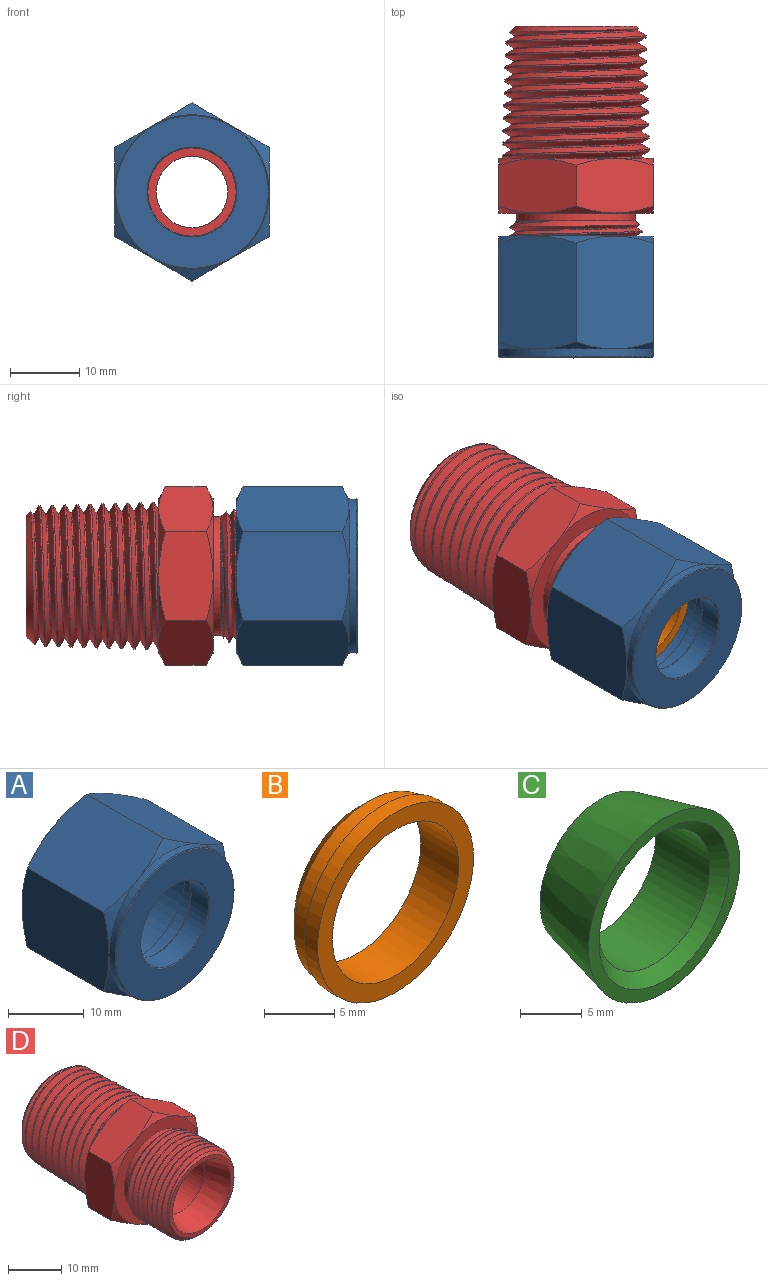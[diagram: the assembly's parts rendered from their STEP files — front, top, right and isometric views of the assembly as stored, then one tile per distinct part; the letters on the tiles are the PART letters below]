
ASSEMBLY  parts=4 mates=3
PART A: 29 faces, bbox 25.7x17.5x25.7 mm
  f0: plane 22.23x22.23mm, normal (0,1,0), area 102.9mm2, adj f2,f3,f4,f5,f6,f7,f22
  f1: plane 21.97x21.97mm, normal (0,-1,0), area 247.3mm2, adj f27,f28
  f2: cone r=12.83mm half-angle=60deg, axis (0,-1,0), area 7.7mm2, adj f0,f9,f10
  f3: cone r=12.83mm half-angle=60deg, axis (0,-1,0), area 7.7mm2, adj f0,f10,f11
  f4: cone r=12.83mm half-angle=60deg, axis (0,-1,0), area 7.7mm2, adj f0,f11,f12
  f5: cone r=12.83mm half-angle=60deg, axis (0,-1,0), area 7.7mm2, adj f0,f12,f13
  f6: cone r=12.83mm half-angle=60deg, axis (0,-1,0), area 7.7mm2, adj f0,f8,f13
  f7: cone r=12.83mm half-angle=60deg, axis (0,-1,0), area 7.7mm2, adj f0,f8,f9
  f8: plane 16.26x11.11mm, normal (0.5,0,0.87), area 199.9mm2, adj f6,f7,f9,f13,f15,f20
  f9: plane 16.26x12.84mm, normal (1,0,0), area 199.9mm2, adj f2,f7,f8,f10,f19,f20
  f10: plane 16.26x11.11mm, normal (0.5,0,-0.87), area 199.9mm2, adj f2,f3,f9,f11,f18,f19
  f11: plane 16.26x11.11mm, normal (-0.5,0,-0.87), area 199.9mm2, adj f3,f4,f10,f12,f17,f18
  f12: plane 16.26x12.84mm, normal (-1,0,0), area 199.9mm2, adj f4,f5,f11,f13,f16,f17
  f13: plane 16.26x11.11mm, normal (-0.5,0,0.87), area 199.9mm2, adj f5,f6,f8,f12,f15,f16
  f14: cylinder r=11.11mm len=22.23mm, axis (0,-1,0), area 79.8mm2, adj f15,f16,f17,f18,f19,f20,f28
  f15: cone r=11.11mm half-angle=60deg, axis (0,1,0), area 7.7mm2, adj f8,f13,f14
  f16: cone r=11.11mm half-angle=60deg, axis (0,1,0), area 7.7mm2, adj f12,f13,f14
  f17: cone r=11.11mm half-angle=60deg, axis (0,1,0), area 7.7mm2, adj f11,f12,f14
  f18: cone r=11.11mm half-angle=60deg, axis (0,1,0), area 7.7mm2, adj f10,f11,f14
  f19: cone r=11.11mm half-angle=60deg, axis (0,1,0), area 7.7mm2, adj f9,f10,f14
  f20: cone r=11.11mm half-angle=60deg, axis (0,1,0), area 7.7mm2, adj f8,f9,f14
  f21: cylinder r=6.35mm len=12.7mm, axis (0,-1,0), area 129.7mm2, adj f26,f27
  f22: cylinder r=9.53mm len=19.05mm, axis (0,-1,0), area 629.3mm2, adj f0,f23
  f23: plane 19.05x19.05mm, normal (0,1,0), area 36.7mm2, adj f22,f24
  f24: cylinder r=8.89mm len=17.78mm, axis (0,-1,0), area 195.8mm2, adj f23,f25
  f25: plane 17.78x17.78mm, normal (0,1,0), area 116.5mm2, adj f24,f26
  f26: cone r=6.48mm half-angle=45deg, axis (0,1,0), area 7.2mm2, adj f21,f25
  f27: cone r=6.35mm half-angle=45deg, axis (0,-1,0), area 7.2mm2, adj f1,f21
  f28: cone r=10.99mm half-angle=45deg, axis (0,1,0), area 12.5mm2, adj f1,f14
PART B: 6 faces, bbox 15.7x3.8x15.7 mm
  f0: plane 15.67x15.67mm, normal (0,-1,0), area 66.2mm2, adj f1,f5
  f1: cylinder r=7.84mm len=15.67mm, axis (0,-1,0), area 62.5mm2, adj f0,f2
  f2: plane 15.67x15.67mm, normal (0,1,0), area 17.7mm2, adj f1,f3
  f3: cylinder r=7.47mm len=14.94mm, axis (0,-1,0), area 66.7mm2, adj f2,f4
  f4: cone r=6.35mm half-angle=45deg, axis (0,-1,0), area 68.6mm2, adj f3,f5
  f5: cylinder r=6.35mm len=12.7mm, axis (0,-1,0), area 152mm2, adj f0,f4
PART C: 5 faces, bbox 17.3x7.3x17.3 mm
  f0: cone r=6.88mm half-angle=13.7deg, axis (0,-1,0), area 367.6mm2, adj f1,f4
  f1: plane 17.32x17.32mm, normal (0,-1,0), area 60.5mm2, adj f0,f2
  f2: cone r=7.47mm half-angle=45deg, axis (0,-1,0), area 68.6mm2, adj f1,f3
  f3: cylinder r=6.35mm len=12.7mm, axis (0,-1,0), area 247.3mm2, adj f2,f4
  f4: plane 13.77x13.77mm, normal (0,1,0), area 22.2mm2, adj f0,f3
PART D: 41 faces, bbox 26.7x41x26.7 mm
  f0: cylinder r=5.16mm len=10.31mm, axis (0,-1,0), area 151.1mm2, adj f34,f40
  f1: plane 17.35x17.35mm, normal (0,1,0), area 40.4mm2, adj f37,f39
  f2: cone r=10.05mm half-angle=1.8deg, axis (0,-1,0), area 170.7mm2, adj f4,f5,f7,f37,f38
  f3: bspline ~19.45x19.06mm, area 135.9mm2, adj f4,f5,f7,f37
  f4: bspline ~21.6x21.57mm, area 804.9mm2, adj f2,f3,f7,f37
  f5: bspline ~21.65x21.62mm, area 840mm2, adj f2,f3,f7,f37,f38
  f6: plane 17.13x17.13mm, normal (0,-1,0), area 44.2mm2, adj f11,f36
  f7: plane 22.91x22.91mm, normal (0,1,0), area 68.5mm2, adj f2,f3,f4,f5,f28,f29,f30,f31
  f8: plane 22.23x22.23mm, normal (0,-1,0), area 157.6mm2, adj f10,f16,f17,f18,f19,f20,f21
  f9: cone r=9.66mm half-angle=45deg, axis (0,-1,0), area 43.5mm2, adj f10,f12,f13,f14,f15
  f10: cylinder r=8.56mm len=17.13mm, axis (0,-1,0), area 59.2mm2, adj f8,f9
  f11: cone r=8.56mm half-angle=45deg, axis (0,1,0), area 43.6mm2, adj f6,f12,f13,f14,f15
  f12: bspline ~19.19x19.19mm, area 418.2mm2, adj f9,f11,f13,f15
  f13: cylinder r=8.7mm len=17.4mm, axis (0,-1,0), area 72.3mm2, adj f9,f11,f12,f14
  f14: bspline ~19.19x19.19mm, area 418mm2, adj f9,f11,f13,f15
  f15: cylinder r=9.53mm len=19.05mm, axis (0,1,0), area 66.9mm2, adj f9,f11,f12,f14
  f16: cone r=11.11mm half-angle=60deg, axis (0,1,0), area 12.1mm2, adj f8,f25,f26
  f17: cone r=11.11mm half-angle=60deg, axis (0,1,0), area 12.1mm2, adj f8,f24,f25
  f18: cone r=11.11mm half-angle=60deg, axis (0,1,0), area 12.1mm2, adj f8,f23,f24
  f19: cone r=11.11mm half-angle=60deg, axis (0,1,0), area 12.1mm2, adj f8,f22,f23
  f20: cone r=11.11mm half-angle=60deg, axis (0,1,0), area 12.1mm2, adj f8,f22,f27
  f21: cone r=11.11mm half-angle=60deg, axis (0,1,0), area 12.1mm2, adj f8,f26,f27
  f22: plane 12.17x8.93mm, normal (0.5,0,0.87), area 92.3mm2, adj f19,f20,f23,f27,f31,f32
  f23: plane 13.9x8.94mm, normal (1,0,0), area 92.3mm2, adj f18,f19,f22,f24,f30,f31
  f24: plane 12.17x8.93mm, normal (0.5,0,-0.87), area 92.3mm2, adj f17,f18,f23,f25,f29,f30
  f25: plane 12.17x8.93mm, normal (-0.5,0,-0.87), area 92.3mm2, adj f16,f17,f24,f26,f28,f29
  f26: plane 13.9x8.94mm, normal (-1,0,0), area 92.3mm2, adj f16,f21,f25,f27,f28,f33
  f27: plane 12.17x8.93mm, normal (-0.5,0,0.87), area 92.3mm2, adj f20,f21,f22,f26,f32,f33
  f28: cone r=12.83mm half-angle=60deg, axis (0,-1,0), area 12.1mm2, adj f7,f25,f26
  f29: cone r=12.83mm half-angle=60deg, axis (0,-1,0), area 12.1mm2, adj f7,f24,f25
  f30: cone r=12.83mm half-angle=60deg, axis (0,-1,0), area 12.1mm2, adj f7,f23,f24
  f31: cone r=12.83mm half-angle=60deg, axis (0,-1,0), area 12.1mm2, adj f7,f22,f23
  f32: cone r=12.83mm half-angle=60deg, axis (0,-1,0), area 12.1mm2, adj f7,f22,f27
  f33: cone r=12.83mm half-angle=60deg, axis (0,-1,0), area 12.1mm2, adj f7,f26,f27
  f34: plane 12.7x12.7mm, normal (0,-1,0), area 43.2mm2, adj f0,f35
  f35: cylinder r=6.35mm len=12.7mm, axis (0,-1,0), area 285.4mm2, adj f34,f36
  f36: cone r=6.35mm half-angle=13.7deg, axis (0,-1,0), area 252mm2, adj f6,f35
  f37: cone r=10.25mm half-angle=45deg, axis (0,-1,0), area 67.9mm2, adj f1,f2,f3,f4,f5,f38
  f38: cone r=10.25mm half-angle=45deg, axis (0,-1,0), area 0.2mm2, adj f2,f5,f37
  f39: cylinder r=7.9mm len=19.85mm, axis (0,-1,0), area 985.2mm2, adj f1,f40
  f40: cone r=7.9mm half-angle=59deg, axis (0,1,0), area 131.3mm2, adj f0,f39
PLACE A t=(-10.58,-22.64,10.47)mm
PLACE B t=(-10.58,-18.52,10.47)mm
PLACE C t=(-10.58,-17.17,10.47)mm
PLACE D t=(-10.58,-23.91,10.47)mm
MATE fastened C.f0 <-> D.f0  axis (0,-1,0) through (-10.58,-10.97,10.47)mm
MATE fastened A.f2 <-> B.f1  axis (0,-1,0) through (-10.58,-22.64,10.47)mm
MATE fastened B.f1 <-> D.f0  axis (0,1,0) through (-10.58,-13.75,10.47)mm
